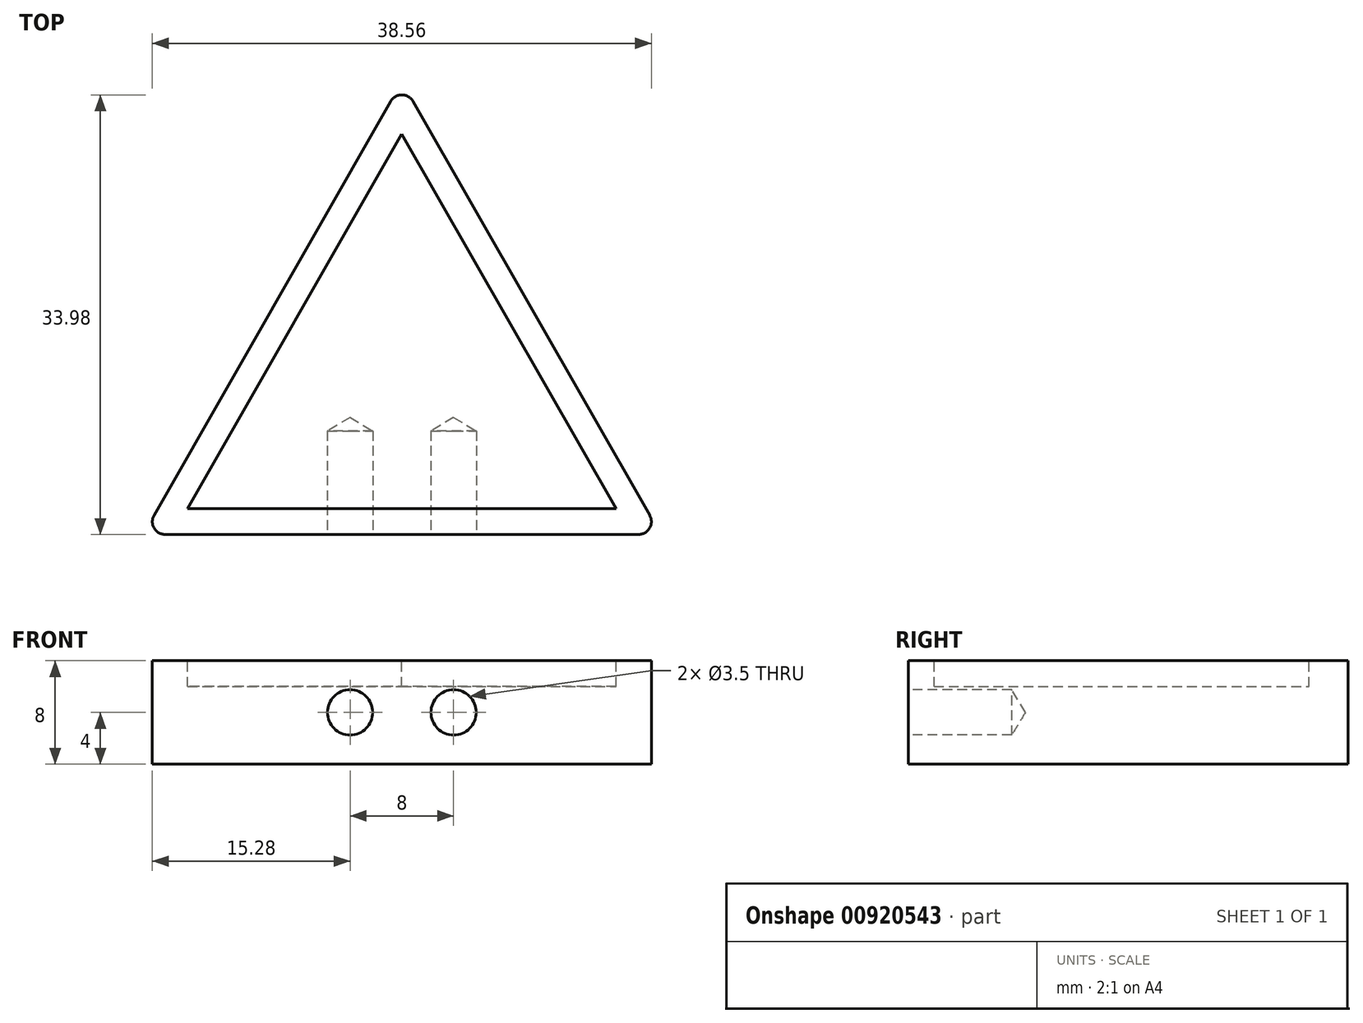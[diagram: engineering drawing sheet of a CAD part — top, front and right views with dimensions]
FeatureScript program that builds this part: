
annotation { "Feature Type Name" : "Feature", "Feature Type Description" : "" }
export const myFeature = defineFeature(function(context is Context, id is Id, definition is map)
    precondition{}
    {
        {
            var Q0;
            Q0=qCreatedBy(makeId("Top.planeOp"),FACE);
            var sketch = newSketch(context, id + "F0", { "sketchPlane" : qUnion([Q0])});
            skLineSegment(sketch, "E0", {"start": v(-20, 0) * mm, "end": v(20, 0) * mm});
            skLineSegment(sketch, "E1", {"start": v(20, 0) * mm, "end": v(0, 35) * mm});
            skLineSegment(sketch, "E2", {"start": v(0, 35) * mm, "end": v(-20, 0) * mm});
            skPoint(sketch, "E3", {"position": v(0, 0) * mm});
            skSolve(sketch);
        }
        {
            var Q0;
            Q0=qSketchRegion(id+"F0",true);
            var Q1;
            Q1=makeQuery(id+"F0.imprint","IMPRINT",FACE,{"disambiguationData":[TD([[makeQuery(id+"F0.imprint","IMPRINT",EDGE,{"derivedFrom":sQuery(id+"F0.wireOp",EDGE,"E0")}),1.0]])]});
            extrude(context, id + "F1", {"entities" : qUnion([Q0, Q1]), "depth" : 8 * mm, "offsetDistance" : 25 * mm});
        }
        {
            var Q0;
            Q0=makeQuery(id+"F1.opExtrude","CAP_FACE",FACE,{"disambiguationData":[OSD([sQuery(id+"F0.wireOp",EDGE,"E0"),sQuery(id+"F0.wireOp",EDGE,"E1"),sQuery(id+"F0.wireOp",EDGE,"E2")])],"isStart":false});
            var sketch = newSketch(context, id + "F2", { "sketchPlane" : qUnion([Q0])});
            skLineSegment(sketch, "E4", {"start": v(-16.55, 2) * mm, "end": v(0, 30.97) * mm});
            skLineSegment(sketch, "E5", {"start": v(0, 30.97) * mm, "end": v(16.55, 2) * mm});
            skLineSegment(sketch, "E6", {"start": v(16.55, 2) * mm, "end": v(-16.55, 2) * mm});
            skSolve(sketch);
        }
        {
            var Q0;
            Q0=makeQuery(id+"F2.imprint","IMPRINT",FACE,{"disambiguationData":[TD([[makeQuery(id+"F2.imprint","IMPRINT",EDGE,{"derivedFrom":sQuery(id+"F2.wireOp",EDGE,"E4")}),-1.0]])]});
            extrude(context, id + "F3", {"entities" : qUnion([Q0]), "operationType" : NewBodyOperationType.REMOVE, "oppositeDirection" : true, "depth" : 2 * mm, "offsetDistance" : 25 * mm});
        }
        {
            var Q0;
            Q0=makeQuery(id+"F1.opExtrude","SWEPT_FACE",FACE,{"disambiguationData":[OSD([sQuery(id+"F0.wireOp",EDGE,"E0")])]});
            var sketch = newSketch(context, id + "F4", { "sketchPlane" : qUnion([Q0])});
            skPoint(sketch, "E7", {"position": v(-4, 4) * mm});
            skPoint(sketch, "E8.MirrorP", {"position": v(4, 4) * mm});
            skSolve(sketch);
        }
        {
            var Q0;
            Q0=sQuery(id+"F4.wireOp",VERTEX,"E7");
            var Q1;
            Q1=sQuery(id+"F4.wireOp",VERTEX,"E8.MirrorP");
            var Q2;
            Q2=makeQuery(id+"F1.opExtrude","SWEPT_BODY",BODY,{"disambiguationData":[OSD([sQuery(id+"F0.wireOp",EDGE,"E0"),sQuery(id+"F0.wireOp",EDGE,"E1"),sQuery(id+"F0.wireOp",EDGE,"E2")])]});
            hole(context, id + "F5", {"style" : HoleStyle.SIMPLE, "endStyle" : HoleEndStyle.BLIND, "holeDiameter" : 3.5 * mm, "majorDiameter" : 5 * mm, "holeDepth" : 8 * mm, "isTappedThrough" : true, "tappedDepth" : 12 * mm, "tapClearance" : 3, "locations" : qUnion([Q0, Q1]), "scope" : qUnion([Q2])});
        }
        {
            var Q0;
            Q0=makeQuery(id+"F1.opExtrude","SWEPT_EDGE",EDGE,{"disambiguationData":[OSD([sQuery(id+"F0.wireOp",EDGE,"E1"),sQuery(id+"F0.wireOp",EDGE,"E2")])]});
            var Q1;
            Q1=makeQuery(id+"F1.opExtrude","SWEPT_EDGE",EDGE,{"disambiguationData":[OSD([sQuery(id+"F0.wireOp",EDGE,"E0"),sQuery(id+"F0.wireOp",EDGE,"E2")])]});
            var Q2;
            Q2=makeQuery(id+"F1.opExtrude","SWEPT_EDGE",EDGE,{"disambiguationData":[OSD([sQuery(id+"F0.wireOp",EDGE,"E0"),sQuery(id+"F0.wireOp",EDGE,"E1")])]});
            fillet(context, id + "F6", {"entities" : qUnion([Q0, Q1, Q2]), "radius" : 1 * mm, "tangentPropagation" : true, "allowEdgeOverflow" : false});
        }
    });
